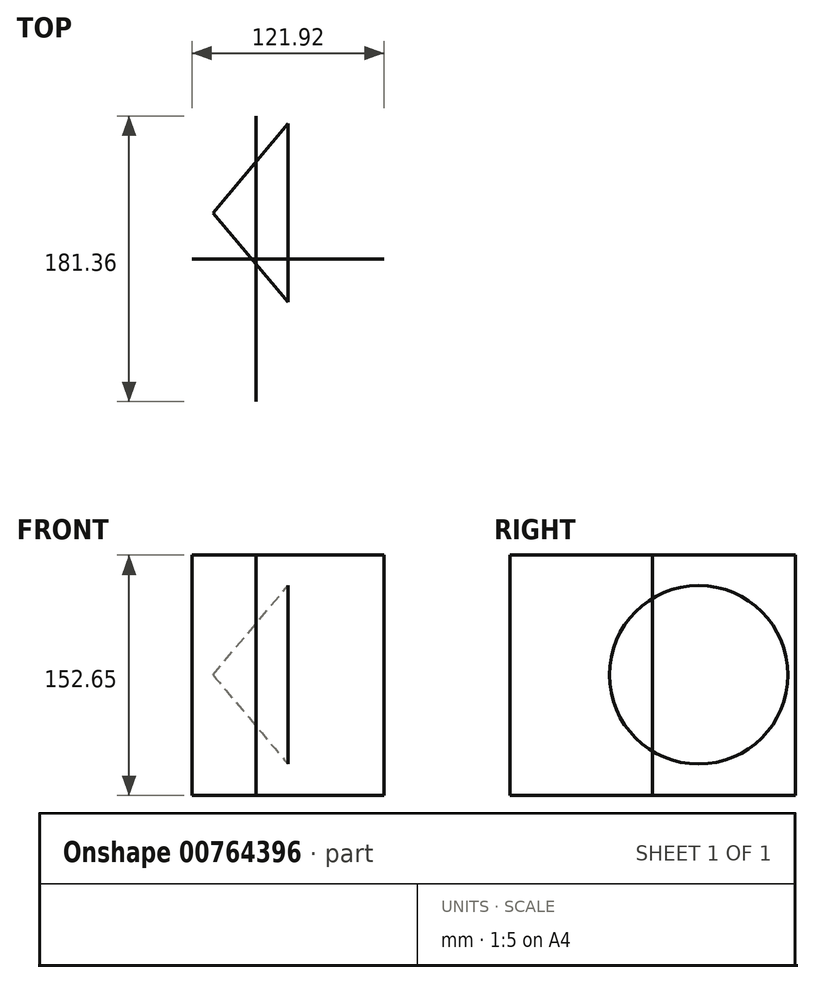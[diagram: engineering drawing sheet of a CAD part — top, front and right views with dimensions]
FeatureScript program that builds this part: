
annotation { "Feature Type Name" : "Feature", "Feature Type Description" : "" }
export const myFeature = defineFeature(function(context is Context, id is Id, definition is map)
    precondition{}
    {
        {
            var Q0;
            Q0=qCreatedBy(makeId("Front.planeOp"),FACE);
            var sketch = newSketch(context, id + "F0", { "sketchPlane" : qUnion([Q0])});
            skLineSegment(sketch, "E0", {"start": v(0, 56.69) * mm, "end": v(-47.66, 0) * mm});
            skLineSegment(sketch, "E1", {"start": v(-47.66, 0) * mm, "end": v(0, 0) * mm});
            skLineSegment(sketch, "E2", {"start": v(0, 0) * mm, "end": v(0, 56.69) * mm});
            skSolve(sketch);
        }
        {
            var Q0;
            Q0=sQuery(id+"F0.wireOp",EDGE,"E0");
            var Q1;
            Q1=sQuery(id+"F0.wireOp",EDGE,"E1");
            revolve(context, id + "F1", {"bodyType" : ToolBodyType.SURFACE, "surfaceOperationType" : NewSurfaceOperationType.NEW, "surfaceEntities" : qUnion([Q0]), "axis" : qUnion([Q1]), "revolveType" : RevolveType.FULL});
        }
        {
            var Q0;
            Q0=qCreatedBy(makeId("Right.planeOp"),FACE);
            var sketch = newSketch(context, id + "F2", { "sketchPlane" : qUnion([Q0])});
            skLineSegment(sketch, "E3", {"start": v(-29.22, 76.05) * mm, "end": v(-29.22, -76.6) * mm});
            skSolve(sketch);
        }
        {
            var Q0;
            Q0 = qSketchRegion(id + "F2", true);
            var Q1;
            Q1=sQuery(id+"F2.wireOp",EDGE,"E3");
            extrude(context, id + "F3", {"entities" : qUnion([Q0]), "bodyType" : ToolBodyType.SURFACE, "surfaceEntities" : qUnion([Q1]), "endBound" : BoundingType.SYMMETRIC, "oppositeDirection" : true, "depth" : 121.92 * mm, "offsetDistance" : 25.4 * mm});
        }
        {
            var Q0;
            Q0=makeQuery(id+"F3.opExtrude","SWEPT_FACE",FACE,{"disambiguationData":[OSD([sQuery(id+"F2.wireOp",EDGE,"E3")])]});
            var sketch = newSketch(context, id + "F4", { "sketchPlane" : qUnion([Q0])});
            skLineSegment(sketch, "E4", {"start": v(20.24, -76.6) * mm, "end": v(20.24, 76.05) * mm});
            skSolve(sketch);
        }
        {
            var Q0;
            Q0=sQuery(id+"F4.wireOp",EDGE,"E4");
            extrude(context, id + "F5", {"bodyType" : ToolBodyType.SURFACE, "surfaceEntities" : qUnion([Q0]), "endBound" : BoundingType.SYMMETRIC, "depth" : 181.36 * mm, "offsetDistance" : 25.4 * mm});
        }
    });
